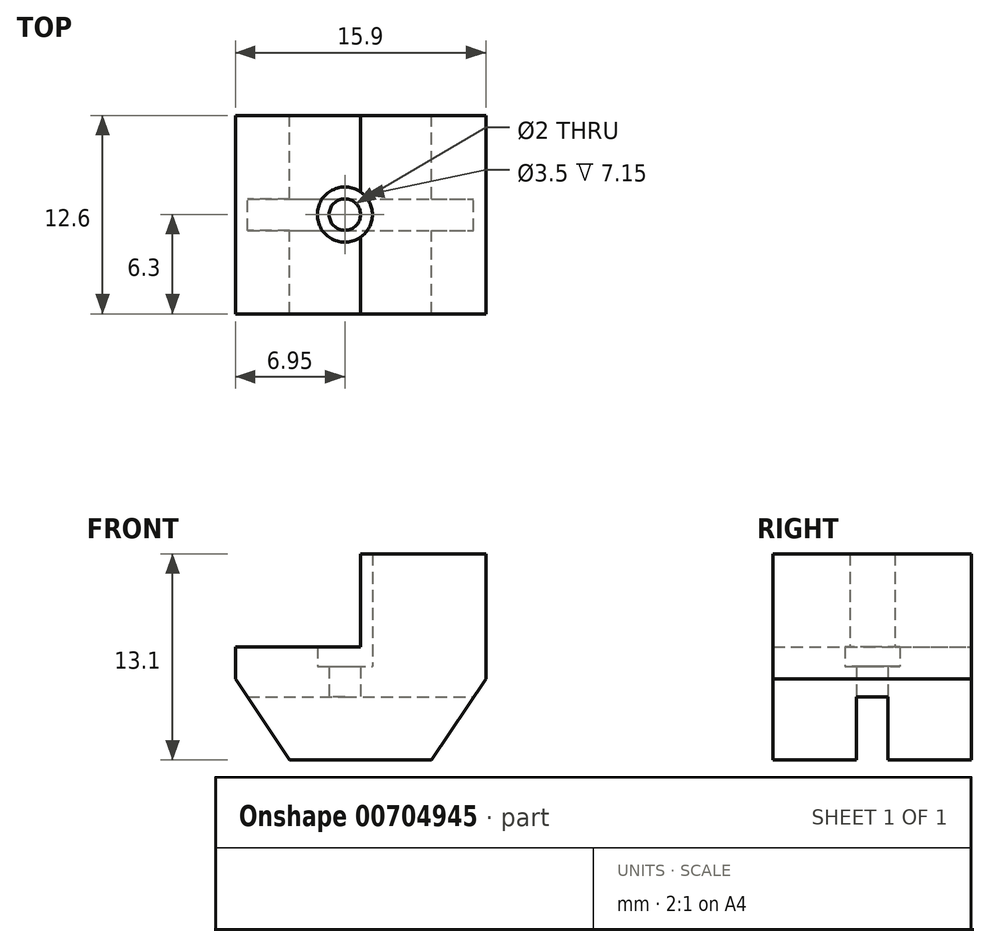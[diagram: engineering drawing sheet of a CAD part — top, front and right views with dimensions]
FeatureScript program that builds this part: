
annotation { "Feature Type Name" : "Feature", "Feature Type Description" : "" }
export const myFeature = defineFeature(function(context is Context, id is Id, definition is map)
    precondition{}
    {
        {
            var Q0;
            Q0=qCreatedBy(makeId("Front.planeOp"),FACE);
            var sketch = newSketch(context, id + "F0", { "sketchPlane" : qUnion([Q0])});
            skLineSegment(sketch, "E0.MirrorCS", {"start": v(0, 7.2) * mm, "end": v(7.95, 7.2) * mm});
            skLineSegment(sketch, "E1", {"start": v(0, 7.2) * mm, "end": v(0, 5.16) * mm});
            skLineSegment(sketch, "E2", {"start": v(0, 5.16) * mm, "end": v(3.45, 0) * mm});
            skLineSegment(sketch, "E3", {"start": v(7.95, 7.2) * mm, "end": v(7.95, 13.1) * mm});
            skLineSegment(sketch, "E4.MirrorCS", {"start": v(15.9, 5.16) * mm, "end": v(12.45, 0) * mm});
            skLineSegment(sketch, "E5.MirrorCS", {"start": v(15.9, 7.2) * mm, "end": v(15.9, 5.16) * mm});
            skLineSegment(sketch, "E6", {"start": v(12.45, 0) * mm, "end": v(3.45, 0) * mm});
            skLineSegment(sketch, "E7", {"start": v(15.9, 7.2) * mm, "end": v(15.9, 13.1) * mm});
            skLineSegment(sketch, "E8", {"start": v(15.9, 13.1) * mm, "end": v(7.95, 13.1) * mm});
            skSolve(sketch);
        }
        {
            var Q0;
            Q0 = qSketchRegion(id + "F0", true);
            extrude(context, id + "F1", {"entities" : qUnion([Q0]), "depth" : 12.6 * mm, "offsetDistance" : 25 * mm});
        }
        {
            var Q0;
            Q0=makeQuery(id+"F1.opExtrude","SWEPT_FACE",FACE,{"disambiguationData":[OSD([sQuery(id+"F0.wireOp",EDGE,"E5.MirrorCS"),sQuery(id+"F0.wireOp",EDGE,"E7")])]});
            var sketch = newSketch(context, id + "F2", { "sketchPlane" : qUnion([Q0])});
            skLineSegment(sketch, "E9", {"start": v(0, 0) * mm, "end": v(-12.6, 0) * mm, "construction": true});
            skPoint(sketch, "E10", {"position": v(-6.3, 0) * mm});
            skLineSegment(sketch, "E11.bottom", {"start": v(-7.3, 0) * mm, "end": v(-5.3, 0) * mm});
            skLineSegment(sketch, "E11.top", {"start": v(-7.3, 4) * mm, "end": v(-5.3, 4) * mm});
            skLineSegment(sketch, "E11.left", {"start": v(-7.3, 0) * mm, "end": v(-7.3, 4) * mm});
            skLineSegment(sketch, "E11.right", {"start": v(-5.3, 0) * mm, "end": v(-5.3, 4) * mm});
            skPoint(sketch, "E11.middle", {"position": v(-6.3, 2) * mm});
            skSolve(sketch);
        }
        {
            var Q0;
            Q0=makeQuery(id+"F2.imprint","IMPRINT",FACE,{"disambiguationData":[TD([[makeQuery(id+"F2.imprint","IMPRINT",EDGE,{"derivedFrom":sQuery(id+"F2.wireOp",EDGE,"E11.bottom")}),1.0]])]});
            extrude(context, id + "F3", {"entities" : qUnion([Q0]), "operationType" : NewBodyOperationType.REMOVE, "endBound" : BoundingType.THROUGH_ALL, "oppositeDirection" : true, "depth" : 25 * mm, "offsetDistance" : 25 * mm});
        }
        {
            var Q0;
            Q0=makeQuery(id+"F1.opExtrude","SWEPT_FACE",FACE,{"disambiguationData":[OSD([sQuery(id+"F0.wireOp",EDGE,"E0.MirrorCS")])]});
            var sketch = newSketch(context, id + "F4", { "sketchPlane" : qUnion([Q0])});
            skPoint(sketch, "E12", {"position": v(6.95, -6.3) * mm});
            skPoint(sketch, "E12.positionSnap0", {"position": v(7.95, -6.3) * mm});
            skSolve(sketch);
        }
        {
            var Q0;
            Q0=sQuery(id+"F4.wireOp",VERTEX,"E12");
            var Q1;
            Q1=makeQuery(id+"F1.opExtrude","SWEPT_BODY",BODY,{"disambiguationData":[OSD([sQuery(id+"F0.wireOp",EDGE,"E0.MirrorCS"),sQuery(id+"F0.wireOp",EDGE,"E1"),sQuery(id+"F0.wireOp",EDGE,"E2"),sQuery(id+"F0.wireOp",EDGE,"E3"),sQuery(id+"F0.wireOp",EDGE,"E4.MirrorCS"),sQuery(id+"F0.wireOp",EDGE,"E5.MirrorCS"),sQuery(id+"F0.wireOp",EDGE,"E6"),sQuery(id+"F0.wireOp",EDGE,"E7"),sQuery(id+"F0.wireOp",EDGE,"E8")])]});
            hole(context, id + "F5", {"style" : HoleStyle.C_BORE, "endStyle" : HoleEndStyle.BLIND, "holeDiameter" : 2 * mm, "cBoreDiameter" : 3.5 * mm, "cBoreDepth" : 1.25 * mm, "majorDiameter" : 5 * mm, "holeDepth" : 38 * mm, "isTappedThrough" : true, "tappedDepth" : 12 * mm, "tapClearance" : 3, "locations" : qUnion([Q0]), "scope" : qUnion([Q1]), "startStyle" : HoleStartStyle.PART});
        }
    });
